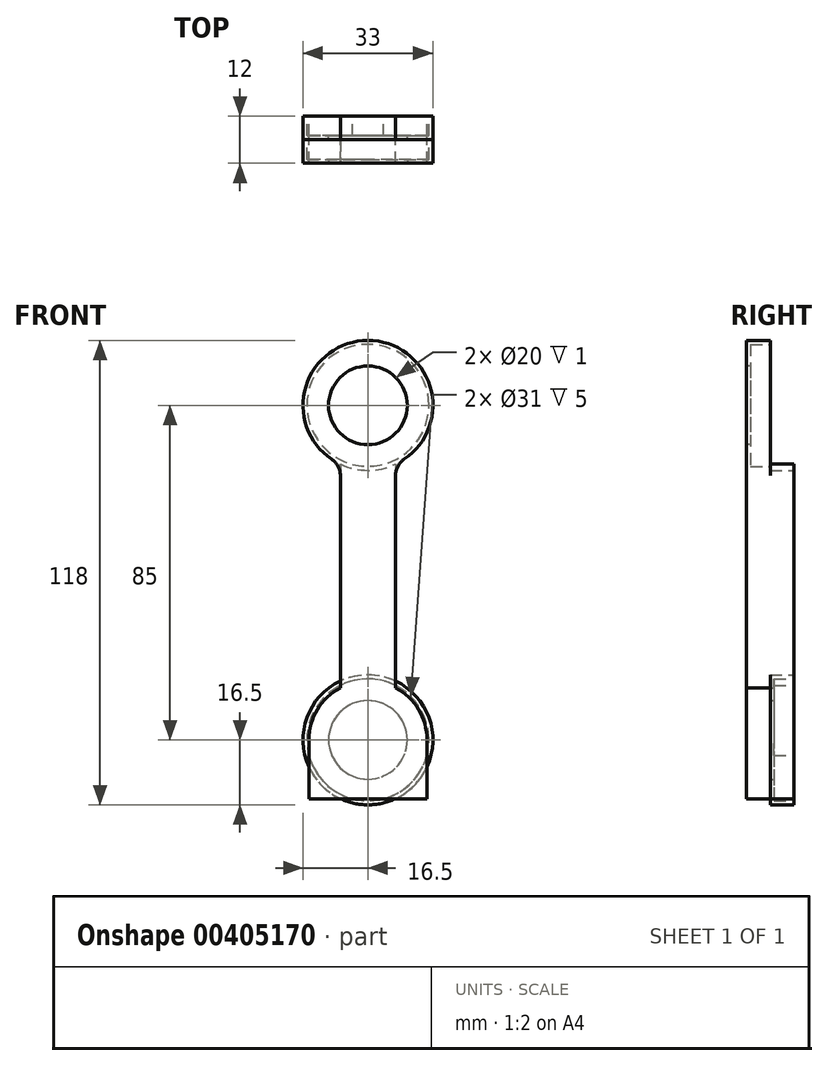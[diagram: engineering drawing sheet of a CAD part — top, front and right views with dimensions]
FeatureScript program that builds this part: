
annotation { "Feature Type Name" : "Feature", "Feature Type Description" : "" }
export const myFeature = defineFeature(function(context is Context, id is Id, definition is map)
    precondition{}
    {
        {
            var Q0;
            Q0=qCreatedBy(makeId("Front.planeOp"),FACE);
            var sketch = newSketch(context, id + "F0", { "sketchPlane" : qUnion([Q0])});
            skArc(sketch, "E0", {"start": v(15, 0) * mm, "mid": v(12.85, 7.75) * mm, "end": v(7, 13.27) * mm});
            skLineSegment(sketch, "E1.left", {"start": v(-7, 70.06) * mm, "end": v(-7, 13.27) * mm});
            skLineSegment(sketch, "E1.right", {"start": v(7, 70.06) * mm, "end": v(7, 13.27) * mm});
            skArc(sketch, "E2", {"start": v(7, 70.06) * mm, "mid": v(0, 101.5) * mm, "end": v(-7, 70.06) * mm});
            skLineSegment(sketch, "E3.top", {"start": v(-15, -15) * mm, "end": v(15, -15) * mm});
            skLineSegment(sketch, "E3.left", {"start": v(-15, 0) * mm, "end": v(-15, -15) * mm});
            skLineSegment(sketch, "E3.right", {"start": v(15, 0) * mm, "end": v(15, -15) * mm});
            skArc(sketch, "E4.trimOffspring", {"start": v(-7, 13.27) * mm, "mid": v(-12.85, 7.75) * mm, "end": v(-15, 0) * mm});
            skSolve(sketch);
        }
        {
            var Q0;
            Q0=makeQuery(id+"F0.imprint","IMPRINT",FACE,{"disambiguationData":[TD([[makeQuery(id+"F0.imprint","IMPRINT",EDGE,{"derivedFrom":sQuery(id+"F0.wireOp",EDGE,"E0")}),1.0]])]});
            extrude(context, id + "F1", {"entities" : qUnion([Q0]), "depth" : 12 * mm});
        }
        {
            var Q0;
            Q0=makeQuery(id+"F1.opExtrude","CAP_FACE",FACE,{"disambiguationData":[OSD([sQuery(id+"F0.wireOp",EDGE,"E0"),sQuery(id+"F0.wireOp",EDGE,"E1.left"),sQuery(id+"F0.wireOp",EDGE,"E1.right"),sQuery(id+"F0.wireOp",EDGE,"E2"),sQuery(id+"F0.wireOp",EDGE,"E3.top"),sQuery(id+"F0.wireOp",EDGE,"E3.left"),sQuery(id+"F0.wireOp",EDGE,"E3.right"),sQuery(id+"F0.wireOp",EDGE,"E4.trimOffspring")])],"isStart":false});
            var sketch = newSketch(context, id + "F2", { "sketchPlane" : qUnion([Q0])});
            skCircle(sketch, "E5", {"center": v(0, 85) * mm, "radius": 10 * mm});
            skSolve(sketch);
        }
        {
            var Q0;
            Q0 = qSketchRegion(id + "F2", true);
            extrude(context, id + "F3", {"entities" : qUnion([Q0]), "operationType" : NewBodyOperationType.REMOVE, "endBound" : BoundingType.THROUGH_ALL, "oppositeDirection" : true, "depth" : 25 * mm});
        }
        {
            var Q0;
            Q0=makeQuery(id+"F1.opExtrude","CAP_FACE",FACE,{"disambiguationData":[OSD([sQuery(id+"F0.wireOp",EDGE,"E0"),sQuery(id+"F0.wireOp",EDGE,"E1.left"),sQuery(id+"F0.wireOp",EDGE,"E1.right"),sQuery(id+"F0.wireOp",EDGE,"E2"),sQuery(id+"F0.wireOp",EDGE,"E3.top"),sQuery(id+"F0.wireOp",EDGE,"E3.left"),sQuery(id+"F0.wireOp",EDGE,"E3.right"),sQuery(id+"F0.wireOp",EDGE,"E4.trimOffspring")])],"isStart":true});
            var sketch = newSketch(context, id + "F4", { "sketchPlane" : qUnion([Q0])});
            skCircle(sketch, "E6", {"center": v(0, 85) * mm, "radius": 16.5 * mm});
            skSolve(sketch);
        }
        {
            var Q0;
            Q0 = qSketchRegion(id + "F4", true);
            extrude(context, id + "F5", {"entities" : qUnion([Q0]), "operationType" : NewBodyOperationType.REMOVE, "oppositeDirection" : true, "depth" : 6 * mm});
        }
        {
            var Q0;
            Q0=makeQuery(id+"F5.boolean.opBoolean","COPY",FACE,{"derivedFrom":makeQuery(id+"F5.opExtrude","CAP_FACE",FACE,{"disambiguationData":[OSD([sQuery(id+"F4.wireOp",EDGE,"E6")])],"isStart":false})});
            var sketch = newSketch(context, id + "F6", { "sketchPlane" : qUnion([Q0])});
            skCircle(sketch, "E7", {"center": v(0, 85) * mm, "radius": 15.5 * mm});
            skSolve(sketch);
        }
        {
            var Q0;
            Q0 = qSketchRegion(id + "F6", true);
            extrude(context, id + "F7", {"entities" : qUnion([Q0]), "operationType" : NewBodyOperationType.REMOVE, "oppositeDirection" : true, "depth" : 5 * mm});
        }
        {
            var Q0;
            {var subQ0=sQuery(id+"F0.wireOp",EDGE,"E1.right");var subQ1=sQuery(id+"F0.wireOp",EDGE,"E2");Q0=makeQuery(id+"F5.boolean.opBoolean","SPLIT",EDGE,{"disambiguationData":[topologyDisambiguationEdgeConnected([makeQuery(id+"F1.opExtrude","SWEPT_FACE",FACE,{"disambiguationData":[OSD([subQ1])]})])],"derivedFrom":makeQuery(id+"F1.opExtrude","SWEPT_EDGE",EDGE,{"disambiguationData":[OSD([subQ0,subQ1])]})});}
            var Q1;
            {var subQ0=sQuery(id+"F0.wireOp",EDGE,"E1.left");var subQ1=sQuery(id+"F0.wireOp",EDGE,"E2");Q1=makeQuery(id+"F5.boolean.opBoolean","SPLIT",EDGE,{"disambiguationData":[topologyDisambiguationEdgeConnected([makeQuery(id+"F1.opExtrude","SWEPT_FACE",FACE,{"disambiguationData":[OSD([subQ1])]})])],"derivedFrom":makeQuery(id+"F1.opExtrude","SWEPT_EDGE",EDGE,{"disambiguationData":[OSD([subQ0,subQ1])]})});}
            fillet(context, id + "F8", {"entities" : qUnion([Q0, Q1]), "radius" : 5 * mm, "tangentPropagation" : true, "allowEdgeOverflow" : false});
        }
        {
            var Q0;
            Q0=qCreatedBy(makeId("Front.planeOp"),FACE);
            var sketch = newSketch(context, id + "F9", { "sketchPlane" : qUnion([Q0])});
            skCircle(sketch, "E8", {"center": v(0, 0) * mm, "radius": 16.5 * mm});
            skCircle(sketch, "E9", {"center": v(0, 0) * mm, "radius": 10 * mm});
            skSolve(sketch);
        }
        {
            var Q0;
            Q0 = qSketchRegion(id + "F9", true);
            extrude(context, id + "F10", {"entities" : qUnion([Q0]), "depth" : 6 * mm});
        }
        {
            var Q0;
            Q0=makeQuery(id+"F10.opExtrude","CAP_FACE",FACE,{"disambiguationData":[OSD([sQuery(id+"F9.wireOp",EDGE,"E8"),sQuery(id+"F9.wireOp",EDGE,"E9")])],"isStart":true});
            var sketch = newSketch(context, id + "F11", { "sketchPlane" : qUnion([Q0])});
            skCircle(sketch, "E10", {"center": v(0, 0) * mm, "radius": 15.5 * mm});
            skSolve(sketch);
        }
        {
            var Q0;
            Q0 = qSketchRegion(id + "F11", true);
            extrude(context, id + "F12", {"entities" : qUnion([Q0]), "operationType" : NewBodyOperationType.REMOVE, "oppositeDirection" : true, "depth" : 5 * mm});
        }
    });
